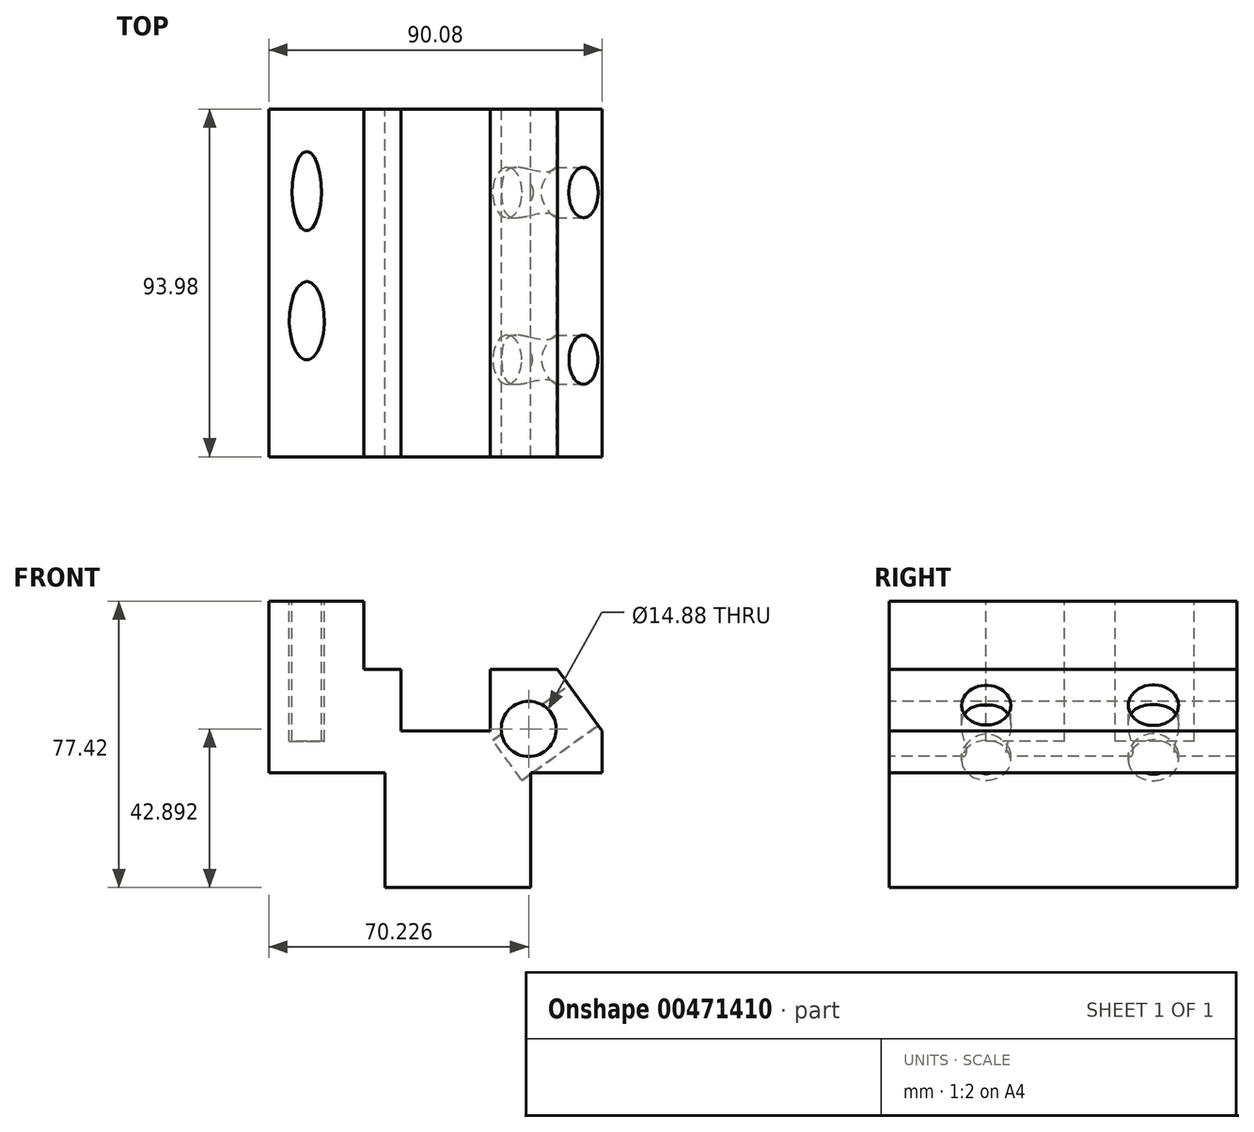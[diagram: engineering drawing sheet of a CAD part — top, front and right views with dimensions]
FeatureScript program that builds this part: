
annotation { "Feature Type Name" : "Feature", "Feature Type Description" : "" }
export const myFeature = defineFeature(function(context is Context, id is Id, definition is map)
    precondition{}
    {
        {
            var Q0;
            Q0=qCreatedBy(makeId("Front.planeOp"),FACE);
            var sketch = newSketch(context, id + "F0", { "sketchPlane" : qUnion([Q0])});
            skLineSegment(sketch, "E0", {"start": v(-59.86, 46.34) * mm, "end": v(-34.25, 46.34) * mm});
            skLineSegment(sketch, "E1", {"start": v(-34.25, 46.34) * mm, "end": v(-34.25, 27.92) * mm});
            skLineSegment(sketch, "E2", {"start": v(-34.25, 27.92) * mm, "end": v(-24.18, 27.92) * mm});
            skLineSegment(sketch, "E3", {"start": v(-24.18, 27.92) * mm, "end": v(-24.18, 11.22) * mm});
            skLineSegment(sketch, "E4", {"start": v(-24.18, 11.22) * mm, "end": v(0, 11.22) * mm});
            skLineSegment(sketch, "E5", {"start": v(0, 11.22) * mm, "end": v(0, 27.92) * mm});
            skLineSegment(sketch, "E6", {"start": v(0, 27.92) * mm, "end": v(18.13, 27.92) * mm});
            skLineSegment(sketch, "E7", {"start": v(18.13, 27.92) * mm, "end": v(30.22, 11.22) * mm});
            skLineSegment(sketch, "E8", {"start": v(30.22, 11.22) * mm, "end": v(30.22, 0) * mm});
            skLineSegment(sketch, "E9", {"start": v(30.22, 0) * mm, "end": v(10.94, 0) * mm});
            skLineSegment(sketch, "E10", {"start": v(10.94, 0) * mm, "end": v(10.94, -31.08) * mm});
            skLineSegment(sketch, "E11", {"start": v(10.94, -31.08) * mm, "end": v(-28.5, -31.08) * mm});
            skLineSegment(sketch, "E12", {"start": v(-28.5, -31.08) * mm, "end": v(-28.5, 0) * mm});
            skLineSegment(sketch, "E13", {"start": v(-28.5, 0) * mm, "end": v(-59.86, 0) * mm});
            skLineSegment(sketch, "E14", {"start": v(-59.86, 0) * mm, "end": v(-59.86, 46.34) * mm});
            skSolve(sketch);
        }
        {
            var Q0;
            Q0 = qSketchRegion(id + "F0", true);
            extrude(context, id + "F1", {"entities" : qUnion([Q0]), "depth" : 93.98 * mm});
        }
        {
            var Q0;
            Q0=makeQuery(id+"F1.opExtrude","SWEPT_FACE",FACE,{"disambiguationData":[OSD([sQuery(id+"F0.wireOp",EDGE,"E7")])]});
            var sketch = newSketch(context, id + "F2", { "sketchPlane" : qUnion([Q0])});
            skCircle(sketch, "E15", {"center": v(-67.73, 0) * mm, "radius": 6.63 * mm});
            skCircle(sketch, "E16", {"center": v(-22.56, 0) * mm, "radius": 6.78 * mm});
            skSolve(sketch);
        }
        {
            var Q0;
            Q0 = qSketchRegion(id + "F2", true);
            extrude(context, id + "F3", {"entities" : qUnion([Q0]), "operationType" : NewBodyOperationType.REMOVE, "oppositeDirection" : true, "depth" : 25.4 * mm});
        }
        {
            var Q0;
            Q0=makeQuery(id+"F1.opExtrude","SWEPT_FACE",FACE,{"disambiguationData":[OSD([sQuery(id+"F0.wireOp",EDGE,"E0")])]});
            var sketch = newSketch(context, id + "F4", { "sketchPlane" : qUnion([Q0])});
            skEllipse(sketch, "E17", {"center": v(-49.61, -22.21) * mm, "majorRadius": 10.72 * mm, "minorRadius": 3.98 * mm, "majorAxis": v(0, 1)});
            skEllipse(sketch, "E18", {"center": v(-49.61, -57.2) * mm, "majorRadius": 10.62 * mm, "minorRadius": 4.72 * mm, "majorAxis": v(0, 1)});
            skSolve(sketch);
        }
        {
            var Q0;
            Q0=makeQuery(id+"F4.imprint","IMPRINT",FACE,{"disambiguationData":[TD([[makeQuery(id+"F4.imprint","IMPRINT",EDGE,{"derivedFrom":sQuery(id+"F4.wireOp",EDGE,"E18")}),1.0]])]});
            var Q1;
            Q1=makeQuery(id+"F4.imprint","IMPRINT",FACE,{"disambiguationData":[TD([[makeQuery(id+"F4.imprint","IMPRINT",EDGE,{"derivedFrom":sQuery(id+"F4.wireOp",EDGE,"E17")}),1.0]])]});
            extrude(context, id + "F5", {"entities" : qUnion([Q0, Q1]), "operationType" : NewBodyOperationType.REMOVE, "oppositeDirection" : true, "depth" : 37.85 * mm});
        }
        {
            var Q0;
            Q0=makeQuery(id+"F1.opExtrude","CAP_FACE",FACE,{"disambiguationData":[OSD([sQuery(id+"F0.wireOp",EDGE,"E0"),sQuery(id+"F0.wireOp",EDGE,"E1"),sQuery(id+"F0.wireOp",EDGE,"E2"),sQuery(id+"F0.wireOp",EDGE,"E3"),sQuery(id+"F0.wireOp",EDGE,"E4"),sQuery(id+"F0.wireOp",EDGE,"E5"),sQuery(id+"F0.wireOp",EDGE,"E6"),sQuery(id+"F0.wireOp",EDGE,"E7"),sQuery(id+"F0.wireOp",EDGE,"E8"),sQuery(id+"F0.wireOp",EDGE,"E9"),sQuery(id+"F0.wireOp",EDGE,"E10"),sQuery(id+"F0.wireOp",EDGE,"E11"),sQuery(id+"F0.wireOp",EDGE,"E12"),sQuery(id+"F0.wireOp",EDGE,"E13"),sQuery(id+"F0.wireOp",EDGE,"E14")])],"isStart":false});
            var sketch = newSketch(context, id + "F6", { "sketchPlane" : qUnion([Q0])});
            skCircle(sketch, "E19", {"center": v(10.37, 11.81) * mm, "radius": 7.44 * mm});
            skSolve(sketch);
        }
        {
            var Q0;
            Q0 = qSketchRegion(id + "F6", true);
            extrude(context, id + "F7", {"entities" : qUnion([Q0]), "operationType" : NewBodyOperationType.REMOVE, "oppositeDirection" : true, "depth" : 128.78 * mm});
        }
    });
